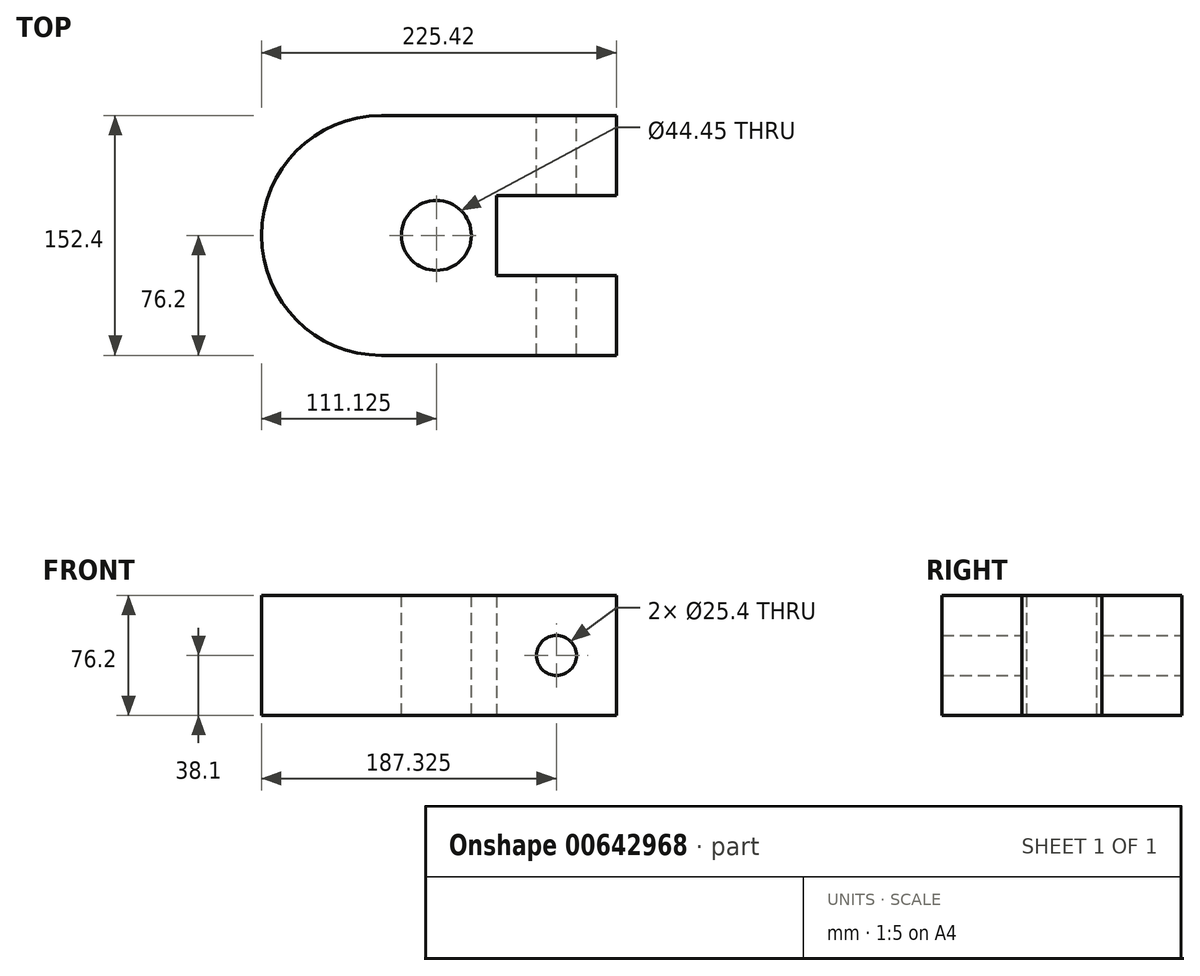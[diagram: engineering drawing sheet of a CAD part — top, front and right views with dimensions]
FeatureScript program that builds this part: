
annotation { "Feature Type Name" : "Feature", "Feature Type Description" : "" }
export const myFeature = defineFeature(function(context is Context, id is Id, definition is map)
    precondition{}
    {
        {
            var Q0;
            Q0=qCreatedBy(makeId("Top.planeOp"),FACE);
            var sketch = newSketch(context, id + "F0", { "sketchPlane" : qUnion([Q0])});
            skLineSegment(sketch, "E0.bottom", {"start": v(0, 0) * mm, "end": v(225.43, 0) * mm});
            skLineSegment(sketch, "E0.top", {"start": v(0, 152.4) * mm, "end": v(225.42, 152.4) * mm});
            skLineSegment(sketch, "E0.left", {"start": v(0, 0) * mm, "end": v(0, 152.4) * mm});
            skLineSegment(sketch, "E1", {"start": v(225.42, 152.4) * mm, "end": v(225.42, 101.6) * mm});
            skLineSegment(sketch, "E2", {"start": v(225.43, 101.6) * mm, "end": v(149.23, 101.6) * mm});
            skLineSegment(sketch, "E3", {"start": v(149.23, 101.6) * mm, "end": v(149.23, 50.8) * mm});
            skLineSegment(sketch, "E4", {"start": v(149.23, 50.8) * mm, "end": v(225.43, 50.8) * mm});
            skLineSegment(sketch, "E5", {"start": v(225.43, 50.8) * mm, "end": v(225.43, 0) * mm});
            skSolve(sketch);
        }
        {
            var Q0;
            Q0 = qSketchRegion(id + "F0", true);
            extrude(context, id + "F1", {"entities" : qUnion([Q0]), "depth" : 76.2 * mm, "offsetDistance" : 25.4 * mm});
        }
        {
            var Q0;
            Q0=makeQuery(id+"F1.opExtrude","SWEPT_EDGE",EDGE,{"disambiguationData":[OSD([sQuery(id+"F0.wireOp",EDGE,"E0.top"),sQuery(id+"F0.wireOp",EDGE,"E0.left")])]});
            fillet(context, id + "F2", {"entities" : qUnion([Q0]), "radius" : 76.2 * mm, "tangentPropagation" : true, "allowEdgeOverflow" : false});
        }
        {
            var Q0;
            Q0=makeQuery(id+"F1.opExtrude","SWEPT_EDGE",EDGE,{"disambiguationData":[OSD([sQuery(id+"F0.wireOp",EDGE,"E0.bottom"),sQuery(id+"F0.wireOp",EDGE,"E0.left")])]});
            fillet(context, id + "F3", {"entities" : qUnion([Q0]), "radius" : 76.2 * mm, "tangentPropagation" : true, "allowEdgeOverflow" : false});
        }
        {
            var Q0;
            Q0=makeQuery(id+"F1.opExtrude","CAP_FACE",FACE,{"disambiguationData":[OSD([sQuery(id+"F0.wireOp",EDGE,"E0.bottom"),sQuery(id+"F0.wireOp",EDGE,"E0.top"),sQuery(id+"F0.wireOp",EDGE,"E0.left"),sQuery(id+"F0.wireOp",EDGE,"E1"),sQuery(id+"F0.wireOp",EDGE,"E2"),sQuery(id+"F0.wireOp",EDGE,"E3"),sQuery(id+"F0.wireOp",EDGE,"E4"),sQuery(id+"F0.wireOp",EDGE,"E5")])],"isStart":false});
            var sketch = newSketch(context, id + "F4", { "sketchPlane" : qUnion([Q0])});
            skCircle(sketch, "E6", {"center": v(111.13, 76.2) * mm, "radius": 22.23 * mm});
            skSolve(sketch);
        }
        {
            var Q0;
            Q0=makeQuery(id+"F1.opExtrude","SWEPT_FACE",FACE,{"disambiguationData":[OSD([sQuery(id+"F0.wireOp",EDGE,"E0.top")])]});
            var sketch = newSketch(context, id + "F5", { "sketchPlane" : qUnion([Q0])});
            skCircle(sketch, "E7", {"center": v(-187.32, 38.1) * mm, "radius": 12.7 * mm});
            skSolve(sketch);
        }
        {
            var Q0;
            Q0=makeQuery(id+"F5.imprint","IMPRINT",FACE,{"disambiguationData":[TD([[makeQuery(id+"F5.imprint","IMPRINT",EDGE,{"derivedFrom":sQuery(id+"F5.wireOp",EDGE,"E7")}),1.0]])]});
            extrude(context, id + "F6", {"entities" : qUnion([Q0]), "operationType" : NewBodyOperationType.REMOVE, "oppositeDirection" : true, "depth" : 152.4 * mm, "offsetDistance" : 25.4 * mm});
        }
        {
            var Q0;
            Q0=makeQuery(id+"F4.imprint","IMPRINT",FACE,{"disambiguationData":[TD([[makeQuery(id+"F4.imprint","IMPRINT",EDGE,{"derivedFrom":sQuery(id+"F4.wireOp",EDGE,"E6")}),1.0]])]});
            extrude(context, id + "F7", {"entities" : qUnion([Q0]), "operationType" : NewBodyOperationType.REMOVE, "oppositeDirection" : true, "depth" : 76.2 * mm, "offsetDistance" : 25.4 * mm});
        }
    });
